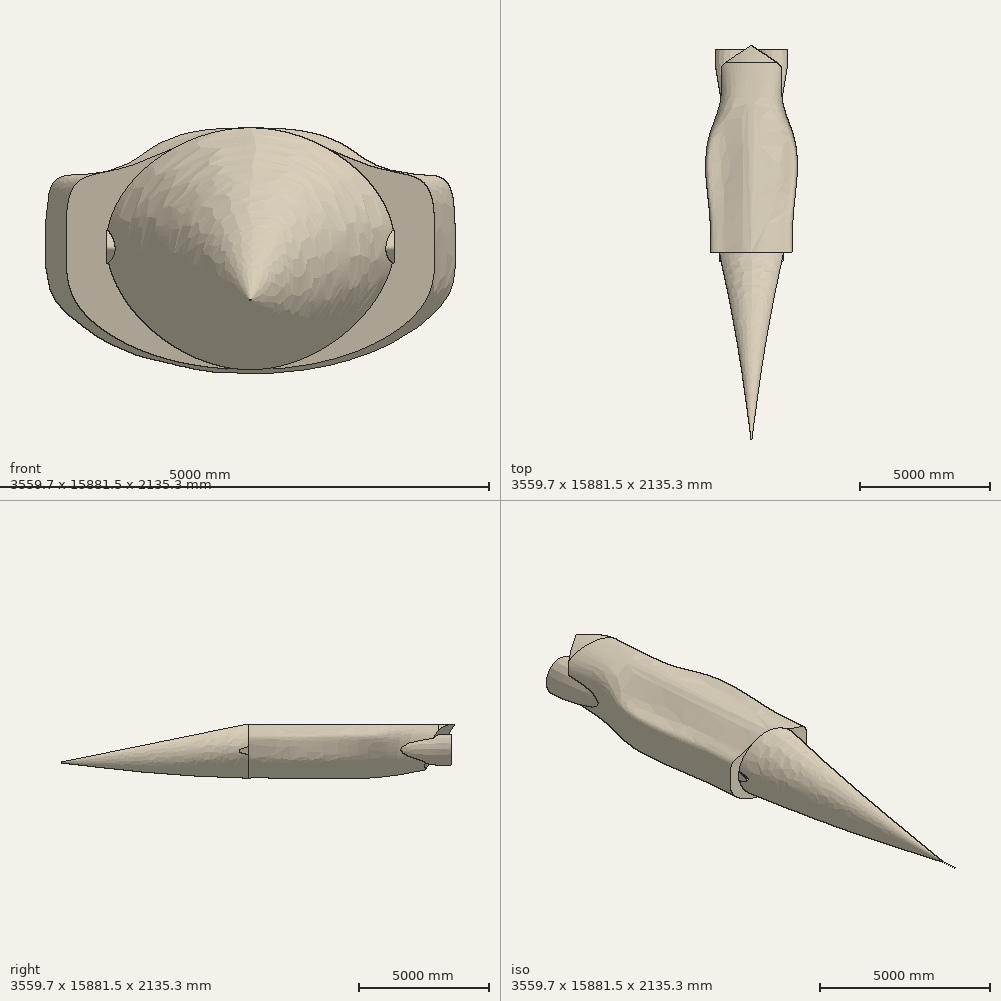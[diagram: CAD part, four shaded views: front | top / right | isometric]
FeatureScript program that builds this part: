
annotation { "Feature Type Name" : "Feature", "Feature Type Description" : "" }
export const myFeature = defineFeature(function(context is Context, id is Id, definition is map)
    precondition{}
    {
        {
            var Q0;
            Q0=qCreatedBy(makeId("Right.planeOp"),FACE);
            var sketch = newSketch(context, id + "F0", { "sketchPlane" : qUnion([Q0])});
            skLineSegment(sketch, "E0", {"start": v(0, 0) * mm, "end": v(-1750, 0) * mm});
            skLineSegment(sketch, "E1", {"start": v(-1750, 0) * mm, "end": v(-3500, 0) * mm});
            skLineSegment(sketch, "E2", {"start": v(-3500, 0) * mm, "end": v(-3500, -1000) * mm});
            skLineSegment(sketch, "E3", {"start": v(-3500, -1000) * mm, "end": v(-8500, -1000) * mm});
            skLineSegment(sketch, "E4", {"start": v(-8500, -1000) * mm, "end": v(-8500, -499.31) * mm});
            skLineSegment(sketch, "E5", {"start": v(-1151.4, 0) * mm, "end": v(-1151.4, 1000) * mm});
            skLineSegment(sketch, "E6", {"start": v(-1151.4, 1000) * mm, "end": v(-8500, -499.31) * mm});
            skLineSegment(sketch, "E7", {"start": v(-8500, -499.31) * mm, "end": v(-3500, -1000) * mm});
            skLineSegment(sketch, "E8", {"start": v(-3500, 0) * mm, "end": v(-3500, 520.82) * mm});
            skLineSegment(sketch, "E9", {"start": v(-8500, -499.31) * mm, "end": v(-8450, -499.31) * mm});
            skLineSegment(sketch, "E10", {"start": v(-8450, -499.31) * mm, "end": v(-8450, -489.1) * mm});
            skLineSegment(sketch, "E11", {"start": v(-8450, -499.31) * mm, "end": v(-8450, -504.32) * mm});
            skSolve(sketch);
        }
        {
            var Q0;
            Q0=sQuery(id+"F0.wireOp",EDGE,"E5");
            cPlane(context, id + "F1", {"entities" : qUnion([Q0]), "cplaneType" : CPlaneType.LINE_ANGLE, "offset" : 25 * mm, "angle" : 90 * degree, "oppositeDirection" : true, "width" : 150 * mm, "height" : 150 * mm});
        }
        {
            var Q0;
            Q0=qCreatedBy(id+"F1.planeOp",FACE);
            var sketch = newSketch(context, id + "F2", { "sketchPlane" : qUnion([Q0])});
            skPoint(sketch, "E12.middle", {"position": v(0, 0) * mm});
            skFitSpline(sketch, "E13", {"points": [v(0, 1000) * mm, v(-1060, 662.5) * mm, v(-1517.6, 506.84) * mm, v(-1600, 0) * mm, v(-1517.6, -506.84) * mm, v(-750, -1000) * mm, v(750, -1000) * mm, v(1517.6, -506.84) * mm, v(1600, 0) * mm, v(1517.6, 506.84) * mm, v(1060, 662.5) * mm, v(0, 1000) * mm]});
            skSolve(sketch);
        }
        {
            var Q0;
            Q0=qCreatedBy(makeId("Front.planeOp"),FACE);
            var sketch = newSketch(context, id + "F3", { "sketchPlane" : qUnion([Q0])});
            skPoint(sketch, "E14.middle", {"position": v(0, 0) * mm});
            skFitSpline(sketch, "E15", {"points": [v(0, 1000) * mm, v(-1060, 662.5) * mm, v(-1517.6, 506.84) * mm, v(-1600, 0) * mm, v(-1517.6, -506.84) * mm, v(-750, -1000) * mm, v(750, -1000) * mm, v(1517.6, -506.84) * mm, v(1600, 0) * mm, v(1517.6, 506.84) * mm, v(1060, 662.5) * mm, v(0, 1000) * mm]});
            skSolve(sketch);
        }
        {
            var Q0;
            Q0=qCreatedBy(makeId("Front.planeOp"),FACE);
            cPlane(context, id + "F4", {"entities" : qUnion([Q0]), "cplaneType" : CPlaneType.OFFSET, "offset" : 3500 * mm, "oppositeDirection" : true, "width" : 150 * mm, "height" : 150 * mm});
        }
        {
            var Q0;
            Q0=qCreatedBy(id+"F4.planeOp",FACE);
            var sketch = newSketch(context, id + "F5", { "sketchPlane" : qUnion([Q0])});
            skPoint(sketch, "E16.middle", {"position": v(0, 0) * mm});
            skFitSpline(sketch, "E17", {"points": [v(0, 1000) * mm, v(-1060, 662.5) * mm, v(-1517.6, 506.84) * mm, v(-1600, 0) * mm, v(-1517.6, -506.84) * mm, v(-750, -1000) * mm, v(750, -1000) * mm, v(1517.6, -506.84) * mm, v(1600, 0) * mm, v(1517.6, 506.84) * mm, v(1060, 662.5) * mm, v(0, 1000) * mm]});
            skSolve(sketch);
        }
        {
            var Q0;
            Q0=qCreatedBy(makeId("Front.planeOp"),FACE);
            cPlane(context, id + "F6", {"entities" : qUnion([Q0]), "cplaneType" : CPlaneType.OFFSET, "offset" : 4500 * mm, "oppositeDirection" : true, "width" : 150 * mm, "height" : 150 * mm});
        }
        {
            var Q0;
            Q0=qCreatedBy(id+"F6.planeOp",FACE);
            var sketch = newSketch(context, id + "F7", { "sketchPlane" : qUnion([Q0])});
            skPoint(sketch, "E18.middle", {"position": v(0, 0) * mm});
            skFitSpline(sketch, "E19", {"points": [v(0, 1000) * mm, v(-1060, 662.5) * mm, v(-1250, 0) * mm, v(-1060, -662.5) * mm, v(0, -1000) * mm, v(1060, -662.5) * mm, v(1250, 0) * mm, v(1060, 662.5) * mm, v(0, 1000) * mm]});
            skSolve(sketch);
        }
        {
            var Q0;
            Q0=qCreatedBy(makeId("Front.planeOp"),FACE);
            cPlane(context, id + "F8", {"entities" : qUnion([Q0]), "cplaneType" : CPlaneType.OFFSET, "offset" : 6232.05 * mm, "oppositeDirection" : true, "width" : 150 * mm, "height" : 150 * mm});
        }
        {
            var Q0;
            Q0=qCreatedBy(id+"F8.planeOp",FACE);
            var sketch = newSketch(context, id + "F9", { "sketchPlane" : qUnion([Q0])});
            skPoint(sketch, "E20.middle", {"position": v(0, 0) * mm});
            skFitSpline(sketch, "E21", {"points": [v(0, 1000) * mm, v(-1060, 662.5) * mm, v(-1250, 0) * mm, v(-848, -530) * mm, v(848, -530) * mm, v(1250, 0) * mm, v(1060, 662.5) * mm, v(0, 1000) * mm]});
            skSolve(sketch);
        }
        {
            var Q0;
            Q0=makeQuery(id+"F2.imprint","IMPRINT",FACE,{"disambiguationData":[TD([[makeQuery(id+"F2.imprint","IMPRINT",EDGE,{"derivedFrom":sQuery(id+"F2.wireOp",EDGE,"E13")}),1.0]])]});
            var Q1;
            Q1=makeQuery(id+"F3.imprint","IMPRINT",FACE,{"disambiguationData":[TD([[makeQuery(id+"F3.imprint","IMPRINT",EDGE,{"derivedFrom":sQuery(id+"F3.wireOp",EDGE,"E15")}),1.0]])]});
            var Q2;
            Q2=makeQuery(id+"F5.imprint","IMPRINT",FACE,{"disambiguationData":[TD([[makeQuery(id+"F5.imprint","IMPRINT",EDGE,{"derivedFrom":sQuery(id+"F5.wireOp",EDGE,"E17")}),1.0]])]});
            var Q3;
            Q3=makeQuery(id+"F7.imprint","IMPRINT",FACE,{"disambiguationData":[TD([[makeQuery(id+"F7.imprint","IMPRINT",EDGE,{"derivedFrom":sQuery(id+"F7.wireOp",EDGE,"E19")}),1.0]])]});
            var Q4;
            Q4=makeQuery(id+"F9.imprint","IMPRINT",FACE,{"disambiguationData":[TD([[makeQuery(id+"F9.imprint","IMPRINT",EDGE,{"derivedFrom":sQuery(id+"F9.wireOp",EDGE,"E21")}),1.0]])]});
            loft(context, id + "F10", {"sheetProfilesArray" : [{ "sheetProfileEntities" : qUnion([Q0]) }, { "sheetProfileEntities" : qUnion([Q1]) }, { "sheetProfileEntities" : qUnion([Q2]) }, { "sheetProfileEntities" : qUnion([Q3]) }, { "sheetProfileEntities" : qUnion([Q4]) }]});
        }
        {
            var Q0;
            Q0=makeQuery(id+"F10.opLoft","CAP_FACE",FACE,{"disambiguationData":[OSD([makeQuery(id+"F9.imprint","IMPRINT",FACE,{"disambiguationData":[TD([[makeQuery(id+"F9.imprint","IMPRINT",EDGE,{"derivedFrom":sQuery(id+"F9.wireOp",EDGE,"E21")}),1.0]])]})])],"isStart":true});
            extrude(context, id + "F11", {"entities" : qUnion([Q0]), "operationType" : NewBodyOperationType.ADD, "depth" : 649.4 * mm, "offsetDistance" : 25 * mm});
        }
        {
            var Q0;
            Q0=qCreatedBy(makeId("Right.planeOp"),FACE);
            var sketch = newSketch(context, id + "F12", { "sketchPlane" : qUnion([Q0])});
            skLineSegment(sketch, "E22", {"start": v(0, 0) * mm, "end": v(4500, 0) * mm});
            skLineSegment(sketch, "E23", {"start": v(4500, 0) * mm, "end": v(6232.05, 0) * mm});
            skLineSegment(sketch, "E24", {"start": v(4500, 0) * mm, "end": v(4500, 1000) * mm});
            skLineSegment(sketch, "E25", {"start": v(4500, 1000) * mm, "end": v(6881.46, 1000) * mm});
            skLineSegment(sketch, "E26", {"start": v(6881.46, 1000) * mm, "end": v(6881.46, -1000) * mm});
            skLineSegment(sketch, "E27", {"start": v(6881.46, 1000) * mm, "end": v(6232.05, 0) * mm});
            skLineSegment(sketch, "E28", {"start": v(6232.05, 0) * mm, "end": v(5582.64, -1000) * mm});
            skLineSegment(sketch, "E29", {"start": v(5582.64, -1000) * mm, "end": v(6881.46, -1000) * mm});
            skSolve(sketch);
        }
        {
            var Q0;
            Q0=makeQuery(id+"F12.imprint","IMPRINT",FACE,{"disambiguationData":[TD([[makeQuery(id+"F12.imprint","IMPRINT",EDGE,{"derivedFrom":sQuery(id+"F12.wireOp",EDGE,"E26")}),-1.0]])]});
            var Q1;
            Q1=sQuery(id+"F12.wireOp",EDGE,"E25");
            revolve(context, id + "F13", {"operationType" : NewBodyOperationType.REMOVE, "entities" : qUnion([Q0]), "axis" : qUnion([Q1]), "revolveType" : RevolveType.SYMMETRIC, "oppositeDirection" : true, "angle" : 182 * degree});
        }
        {
            var Q0;
            Q0=qCreatedBy(id+"F1.planeOp",FACE);
            var sketch = newSketch(context, id + "F14", { "sketchPlane" : qUnion([Q0])});
            skFitSpline(sketch, "E30", {"points": [v(0, 1000) * mm, v(-1250, 0) * mm, v(0, -1099.92) * mm, v(1250, 0) * mm, v(0, 1000) * mm]});
            skSolve(sketch);
        }
        {
            var Q0;
            Q0=qCreatedBy(makeId("Front.planeOp"),FACE);
            cPlane(context, id + "F15", {"entities" : qUnion([Q0]), "cplaneType" : CPlaneType.OFFSET, "offset" : 3500 * mm, "width" : 150 * mm, "height" : 150 * mm});
        }
        {
            var Q0;
            Q0=qCreatedBy(id+"F15.planeOp",FACE);
            var sketch = newSketch(context, id + "F16", { "sketchPlane" : qUnion([Q0])});
            skCircle(sketch, "E31", {"center": v(0, -239.59) * mm, "radius": 760.41 * mm});
            skSolve(sketch);
        }
        {
            var Q0;
            Q0=qCreatedBy(makeId("Front.planeOp"),FACE);
            cPlane(context, id + "F17", {"entities" : qUnion([Q0]), "cplaneType" : CPlaneType.OFFSET, "offset" : 8450 * mm, "width" : 150 * mm, "height" : 150 * mm});
        }
        {
            var Q0;
            Q0=qCreatedBy(id+"F17.planeOp",FACE);
            var sketch = newSketch(context, id + "F18", { "sketchPlane" : qUnion([Q0])});
            skCircle(sketch, "E32", {"center": v(0, -496.71) * mm, "radius": 7.6 * mm});
            skSolve(sketch);
        }
        {
            var Q1;
            Q1=makeQuery(id+"F18.imprint","IMPRINT",FACE,{"disambiguationData":[TD([[makeQuery(id+"F18.imprint","IMPRINT",EDGE,{"derivedFrom":sQuery(id+"F18.wireOp",EDGE,"E32")}),1.0]])]});
            var Q2;
            Q2=makeQuery(id+"F16.imprint","IMPRINT",FACE,{"disambiguationData":[TD([[makeQuery(id+"F16.imprint","IMPRINT",EDGE,{"derivedFrom":sQuery(id+"F16.wireOp",EDGE,"E31")}),1.0]])]});
            var Q3;
            Q3=makeQuery(id+"F14.imprint","IMPRINT",FACE,{"disambiguationData":[TD([[makeQuery(id+"F14.imprint","IMPRINT",EDGE,{"derivedFrom":sQuery(id+"F14.wireOp",EDGE,"E30")}),1.0]])]});
            loft(context, id + "F19", {"operationType" : NewBodyOperationType.ADD, "sheetProfilesArray" : [{ "sheetProfileEntities" : qUnion([Q1]) }, { "sheetProfileEntities" : qUnion([Q2]) }, { "sheetProfileEntities" : qUnion([Q3]) }]});
        }
        {
            var Q0;
            Q0=makeQuery(id+"F19.opLoft","CAP_FACE",FACE,{"disambiguationData":[OSD([makeQuery(id+"F18.imprint","IMPRINT",FACE,{"disambiguationData":[TD([[makeQuery(id+"F18.imprint","IMPRINT",EDGE,{"derivedFrom":sQuery(id+"F18.wireOp",EDGE,"E32")}),1.0]])]})])],"isStart":true});
            extrude(context, id + "F20", {"entities" : qUnion([Q0]), "operationType" : NewBodyOperationType.ADD, "depth" : 550 * mm, "offsetDistance" : 25 * mm});
        }
        {
            var Q0;
            Q0=qCreatedBy(makeId("Front.planeOp"),FACE);
            cPlane(context, id + "F21", {"entities" : qUnion([Q0]), "cplaneType" : CPlaneType.OFFSET, "offset" : 3500 * mm, "oppositeDirection" : true, "width" : 150 * mm, "height" : 150 * mm});
        }
        {
            var Q0;
            Q0=qCreatedBy(id+"F21.planeOp",FACE);
            var sketch = newSketch(context, id + "F22", { "sketchPlane" : qUnion([Q0])});
            skCircle(sketch, "E33", {"center": v(-800, 0) * mm, "radius": 600 * mm});
            skCircle(sketch, "E34", {"center": v(800, 0) * mm, "radius": 600 * mm});
            skSolve(sketch);
        }
        {
            var Q0;
            Q0=qCreatedBy(makeId("Front.planeOp"),FACE);
            cPlane(context, id + "F23", {"entities" : qUnion([Q0]), "cplaneType" : CPlaneType.OFFSET, "offset" : 4500 * mm, "oppositeDirection" : true, "width" : 150 * mm, "height" : 150 * mm});
        }
        {
            var Q0;
            Q0=qCreatedBy(id+"F23.planeOp",FACE);
            var sketch = newSketch(context, id + "F24", { "sketchPlane" : qUnion([Q0])});
            skCircle(sketch, "E35", {"center": v(-800, 0) * mm, "radius": 400 * mm});
            skCircle(sketch, "E36", {"center": v(800, 0) * mm, "radius": 400 * mm});
            skSolve(sketch);
        }
        {
            var Q0;
            Q0=qCreatedBy(makeId("Front.planeOp"),FACE);
            cPlane(context, id + "F25", {"entities" : qUnion([Q0]), "cplaneType" : CPlaneType.OFFSET, "offset" : 6232.05 * mm, "oppositeDirection" : true, "width" : 150 * mm, "height" : 150 * mm});
        }
        {
            var Q0;
            Q0=qCreatedBy(id+"F25.planeOp",FACE);
            var sketch = newSketch(context, id + "F26", { "sketchPlane" : qUnion([Q0])});
            skCircle(sketch, "E37", {"center": v(-800, 0) * mm, "radius": 600 * mm});
            skCircle(sketch, "E38", {"center": v(800, 0) * mm, "radius": 600 * mm});
            skSolve(sketch);
        }
        {
            var Q0;
            Q0=qCreatedBy(makeId("Front.planeOp"),FACE);
            cPlane(context, id + "F27", {"entities" : qUnion([Q0]), "cplaneType" : CPlaneType.OFFSET, "offset" : 6732.05 * mm, "oppositeDirection" : true, "width" : 150 * mm, "height" : 150 * mm});
        }
        {
            var Q0;
            Q0=qCreatedBy(id+"F27.planeOp",FACE);
            var sketch = newSketch(context, id + "F28", { "sketchPlane" : qUnion([Q0])});
            skCircle(sketch, "E39", {"center": v(-800, 0) * mm, "radius": 600 * mm});
            skCircle(sketch, "E40", {"center": v(800, 0) * mm, "radius": 600 * mm});
            skSolve(sketch);
        }
        {
            var Q0;
            Q0=makeQuery(id+"F22.imprint","IMPRINT",FACE,{"disambiguationData":[TD([[makeQuery(id+"F22.imprint","IMPRINT",EDGE,{"derivedFrom":sQuery(id+"F22.wireOp",EDGE,"E33")}),1.0]])]});
            var Q1;
            Q1=makeQuery(id+"F24.imprint","IMPRINT",FACE,{"disambiguationData":[TD([[makeQuery(id+"F24.imprint","IMPRINT",EDGE,{"derivedFrom":sQuery(id+"F24.wireOp",EDGE,"E35")}),1.0]])]});
            var Q2;
            Q2=makeQuery(id+"F26.imprint","IMPRINT",FACE,{"disambiguationData":[TD([[makeQuery(id+"F26.imprint","IMPRINT",EDGE,{"derivedFrom":sQuery(id+"F26.wireOp",EDGE,"E37")}),1.0]])]});
            var Q3;
            Q3=makeQuery(id+"F28.imprint","IMPRINT",FACE,{"disambiguationData":[TD([[makeQuery(id+"F28.imprint","IMPRINT",EDGE,{"derivedFrom":sQuery(id+"F28.wireOp",EDGE,"E39")}),1.0]])]});
            loft(context, id + "F29", {"sheetProfilesArray" : [{ "sheetProfileEntities" : qUnion([Q0]) }, { "sheetProfileEntities" : qUnion([Q1]) }, { "sheetProfileEntities" : qUnion([Q2]) }, { "sheetProfileEntities" : qUnion([Q3]) }]});
        }
        {
            var Q0;
            Q0=makeQuery(id+"F22.imprint","IMPRINT",FACE,{"disambiguationData":[TD([[makeQuery(id+"F22.imprint","IMPRINT",EDGE,{"derivedFrom":sQuery(id+"F22.wireOp",EDGE,"E34")}),1.0]])]});
            var Q1;
            Q1=makeQuery(id+"F24.imprint","IMPRINT",FACE,{"disambiguationData":[TD([[makeQuery(id+"F24.imprint","IMPRINT",EDGE,{"derivedFrom":sQuery(id+"F24.wireOp",EDGE,"E36")}),1.0]])]});
            var Q2;
            Q2=makeQuery(id+"F26.imprint","IMPRINT",FACE,{"disambiguationData":[TD([[makeQuery(id+"F26.imprint","IMPRINT",EDGE,{"derivedFrom":sQuery(id+"F26.wireOp",EDGE,"E38")}),1.0]])]});
            var Q3;
            Q3=makeQuery(id+"F28.imprint","IMPRINT",FACE,{"disambiguationData":[TD([[makeQuery(id+"F28.imprint","IMPRINT",EDGE,{"derivedFrom":sQuery(id+"F28.wireOp",EDGE,"E40")}),1.0]])]});
            loft(context, id + "F30", {"sheetProfilesArray" : [{ "sheetProfileEntities" : qUnion([Q0]) }, { "sheetProfileEntities" : qUnion([Q1]) }, { "sheetProfileEntities" : qUnion([Q2]) }, { "sheetProfileEntities" : qUnion([Q3]) }]});
        }
        {
            var Q0;
            Q0=qCreatedBy(makeId("Right.planeOp"),FACE);
            var sketch = newSketch(context, id + "F31", { "sketchPlane" : qUnion([Q0])});
            skFitSpline(sketch, "E41", {"points": [v(-1500, -50) * mm, v(0, 250) * mm, v(3000, 0) * mm, v(0, -250) * mm, v(-1500, -50) * mm]});
            skSolve(sketch);
        }
        {
            var Q0;
            Q0 = qSketchRegion(id + "F31", true);
            extrude(context, id + "F32", {"entities" : qUnion([Q0]), "endBound" : BoundingType.SYMMETRIC, "depth" : 2500 * mm, "offsetDistance" : 25 * mm});
        }
    });
